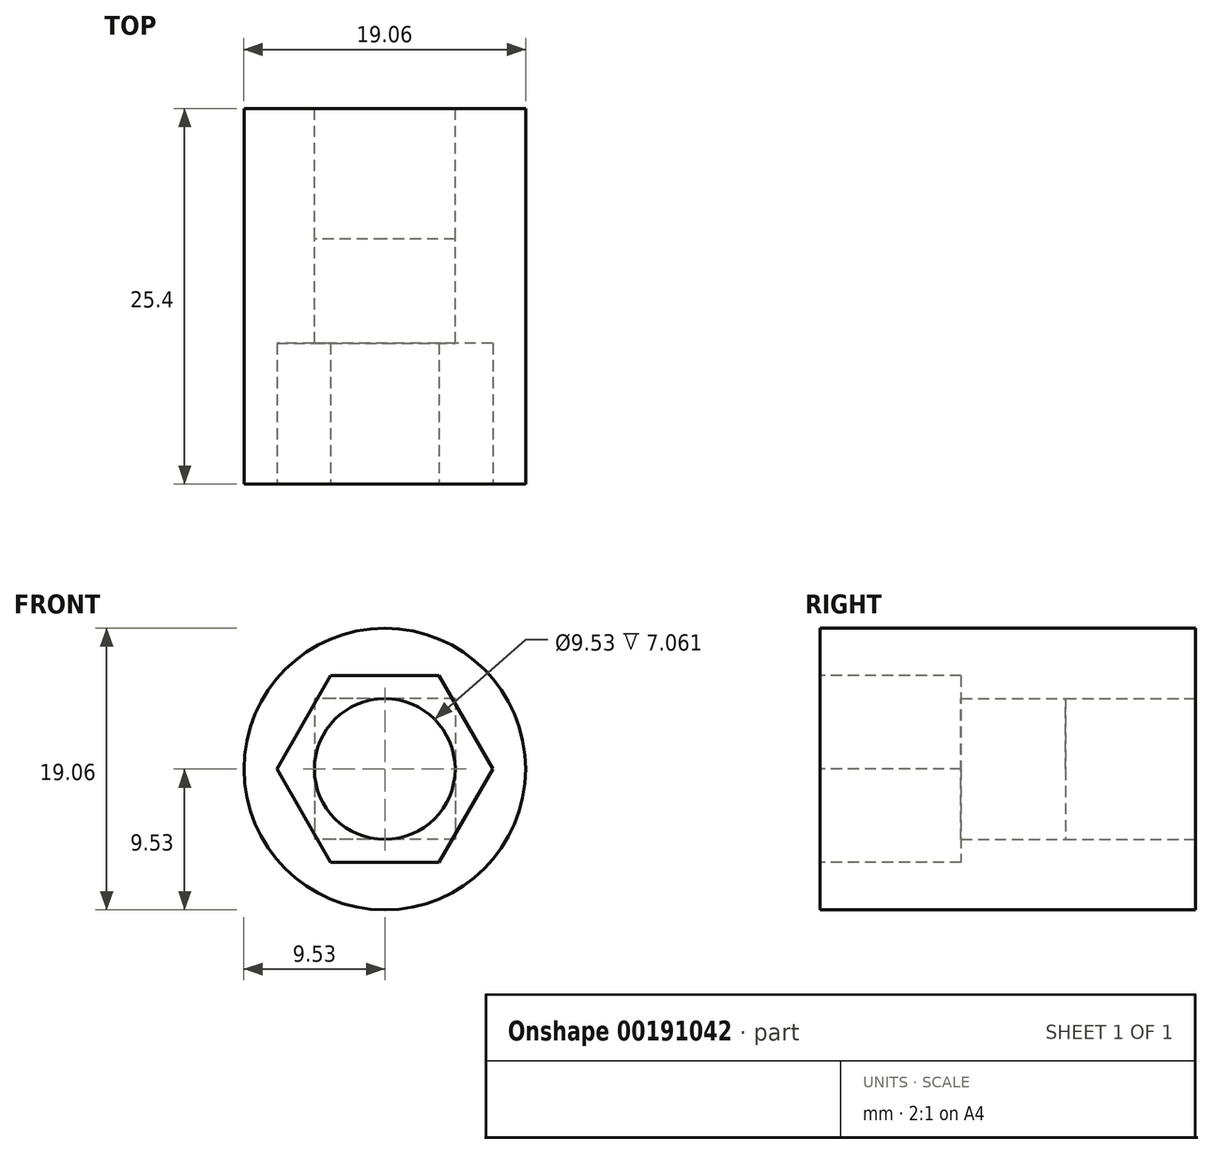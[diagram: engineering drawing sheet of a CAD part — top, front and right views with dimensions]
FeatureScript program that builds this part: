
annotation { "Feature Type Name" : "Feature", "Feature Type Description" : "" }
export const myFeature = defineFeature(function(context is Context, id is Id, definition is map)
    precondition{}
    {
        {
            var Q0;
            Q0=qCreatedBy(makeId("Front.planeOp"),FACE);
            var sketch = newSketch(context, id + "F0", { "sketchPlane" : qUnion([Q0])});
            skCircle(sketch, "E0", {"center": v(0, 0) * mm, "radius": 9.53 * mm});
            skSolve(sketch);
        }
        {
            var Q0;
            Q0 = qSketchRegion(id + "F0", true);
            extrude(context, id + "F1", {"entities" : qUnion([Q0]), "depth" : 25.4 * mm});
        }
        {
            var Q0;
            Q0=qCreatedBy(makeId("Front.planeOp"),FACE);
            var sketch = newSketch(context, id + "F2", { "sketchPlane" : qUnion([Q0])});
            skLineSegment(sketch, "E1.bottom", {"start": v(4.76, 4.76) * mm, "end": v(-4.76, 4.76) * mm});
            skLineSegment(sketch, "E1.top", {"start": v(4.76, -4.76) * mm, "end": v(-4.76, -4.76) * mm});
            skLineSegment(sketch, "E1.left", {"start": v(4.76, 4.76) * mm, "end": v(4.76, -4.76) * mm});
            skLineSegment(sketch, "E1.right", {"start": v(-4.76, 4.76) * mm, "end": v(-4.76, -4.76) * mm});
            skPoint(sketch, "E1.middle", {"position": v(0, 0) * mm});
            skCircle(sketch, "E2", {"center": v(0, 0) * mm, "radius": 4.76 * mm});
            skSolve(sketch);
        }
        {
            var Q0;
            {var subQ0=sQuery(id+"F2.wireOp",EDGE,"E2");var subQ1=makeQuery(id+"F2.imprint","INTERSECT",VERTEX,{"derivedFrom":[sQuery(id+"F2.wireOp",EDGE,"E1.bottom"),subQ0]});Q0=makeQuery(id+"F2.imprint","IMPRINT",FACE,{"disambiguationData":[TD([[makeQuery(id+"F2.imprint","IMPRINT",EDGE,{"disambiguationData":[TD([[subQ1,1.0]])],"derivedFrom":subQ0}),1.0]])]});}
            var Q1;
            Q1=sQuery(id+"F2.wireOp",EDGE,"E2");
            extrude(context, id + "F3", {"entities" : qUnion([Q0]), "operationType" : NewBodyOperationType.REMOVE, "surfaceEntities" : qUnion([Q1]), "depth" : 25.4 * mm});
        }
        {
            var Q0;
            Q0 = qSketchRegion(id + "F2", true);
            var Q1;
            Q1=makeQuery(id+"F1.opExtrude","CAP_FACE",FACE,{"disambiguationData":[OSD([sQuery(id+"F0.wireOp",EDGE,"E0")])],"isStart":false});
            extrude(context, id + "F4", {"entities" : qUnion([Q0, Q1]), "operationType" : NewBodyOperationType.REMOVE, "depth" : 8.8 * mm});
        }
        {
            var Q0;
            Q0=makeQuery(id+"F1.opExtrude","CAP_FACE",FACE,{"disambiguationData":[OSD([sQuery(id+"F0.wireOp",EDGE,"E0")])],"isStart":false});
            var sketch = newSketch(context, id + "F5", { "sketchPlane" : qUnion([Q0])});
            skCircle(sketch, "E3.cCircle", {"center": v(0, 0) * mm, "radius": 6.32 * mm, "construction": true});
            skLineSegment(sketch, "E3.0", {"start": v(3.65, -6.32) * mm, "end": v(-3.65, -6.32) * mm});
            skLineSegment(sketch, "E3.1", {"start": v(-3.65, -6.32) * mm, "end": v(-7.3, 0) * mm});
            skLineSegment(sketch, "E3.2", {"start": v(-7.3, 0) * mm, "end": v(-3.65, 6.32) * mm});
            skLineSegment(sketch, "E3.3", {"start": v(-3.65, 6.32) * mm, "end": v(3.65, 6.32) * mm});
            skLineSegment(sketch, "E3.4", {"start": v(3.65, 6.32) * mm, "end": v(7.3, 0) * mm});
            skLineSegment(sketch, "E3.5", {"start": v(7.3, 0) * mm, "end": v(3.65, -6.32) * mm});
            skPoint(sketch, "E3.0.midPoint", {"position": v(0, -6.32) * mm});
            skSolve(sketch);
        }
        {
            var Q0;
            Q0 = qSketchRegion(id + "F5", true);
            extrude(context, id + "F6", {"entities" : qUnion([Q0]), "operationType" : NewBodyOperationType.REMOVE, "oppositeDirection" : true, "depth" : 9.52 * mm});
        }
    });
